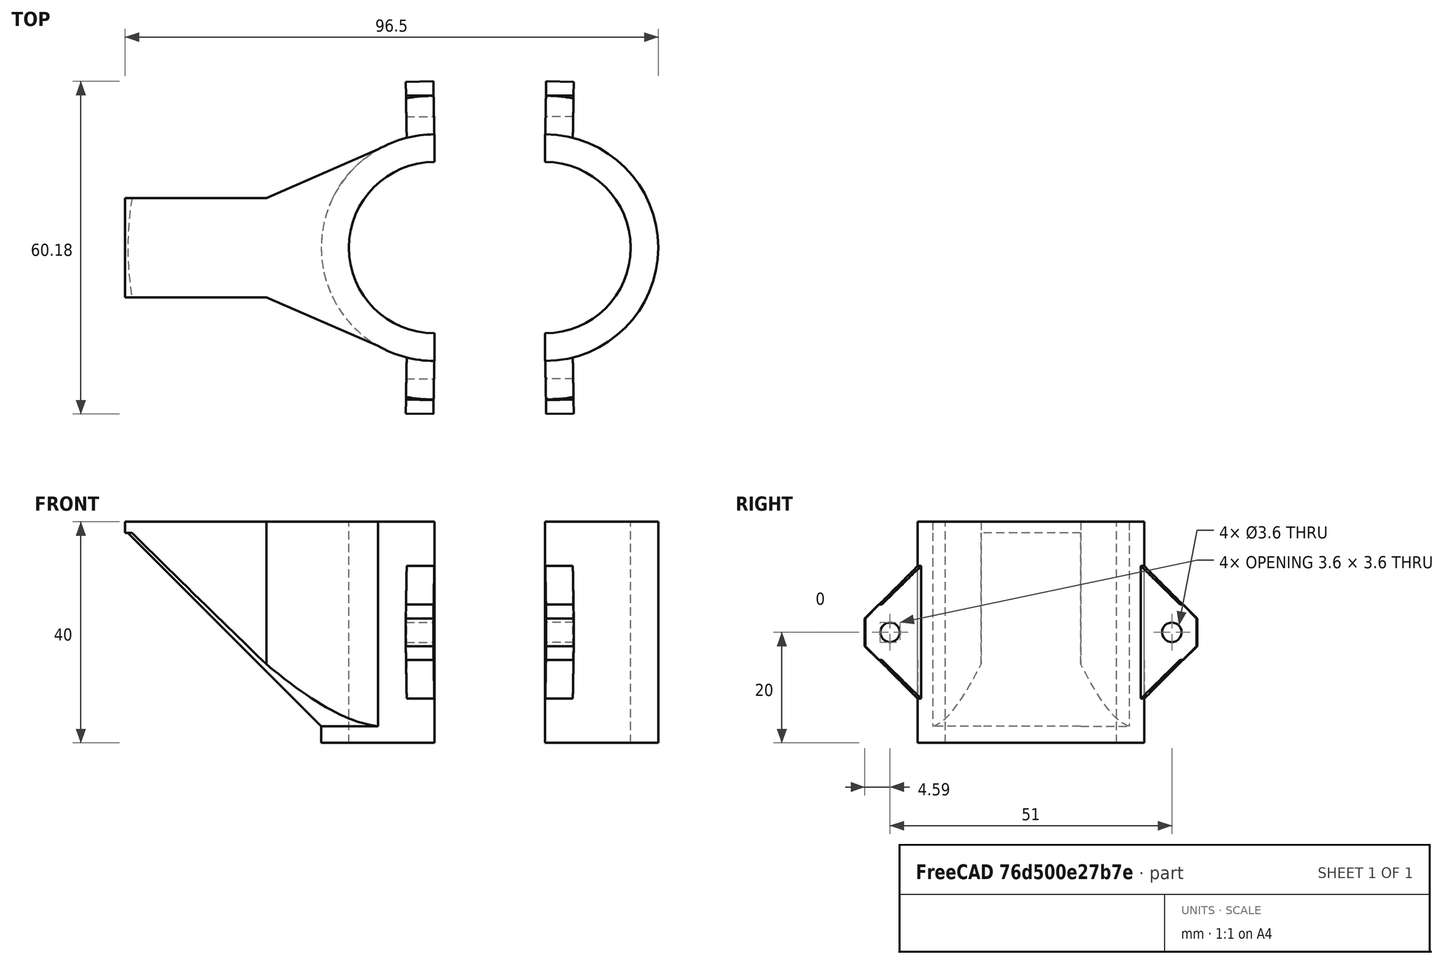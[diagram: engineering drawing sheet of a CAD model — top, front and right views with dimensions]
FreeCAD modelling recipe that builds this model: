
FCSTD DOCUMENT  (FreeCAD 0.17R13528 (Git))
Label: soporteBalda
License: All rights reserved
LicenseURL: http://en.wikipedia.org/wiki/All_rights_reserved
objects: Part::Chamfer×6, Part::Cylinder×3, Part::Cut×3, Part::Box×3, Part::MultiFuse×3, Spreadsheet::Sheet×1
note: 18 computed .brp shape members not serialized (recipe doc carries the construction recipe); baked Part::Feature solids carry a one-line shape summary decoded from their .brp

FEATURE [Spreadsheet::Sheet] Spreadsheet
  cells = A1=Leg diameter; B1(legDiameter)=31; A2=Total height; B2(height)=40
FEATURE [Part::Cylinder] Cylinder  label="Cilindro"
  Angle = 360
  AttacherType = Attacher::AttachEngine3D
  Height = 40
  Radius = 20.5
  expr: Height = Spreadsheet.height
  expr: Radius = Spreadsheet.legDiameter * 0.5 + 5
FEATURE [Part::Cylinder] Cylinder001  label="Cilindro001"
  Angle = 360
  AttacherType = Attacher::AttachEngine3D
  Height = 50
  Placement = pos=(0,0,-5) rot=(0,0,1;0rad)
  Radius = 15.5
  expr: Height = Spreadsheet.height + 10
  expr: Radius = Spreadsheet.legDiameter * 0.5
FEATURE [Part::Cut] Cut
  Base = -> Cylinder
  Tool = -> Cylinder001
FEATURE [Part::Box] Box  label="Cubo"
  AttacherType = Attacher::AttachEngine3D
  Height = 50
  Length = 61
  Placement = pos=(0,-30.5,-5) rot=(0,0,1;0rad)
  Width = 61
  expr: Height = Spreadsheet.height + 10
  expr: Length = Spreadsheet.legDiameter + 30
  expr: Placement.Base.y = -(Spreadsheet.legDiameter + 30) * 0.5
  expr: Width = Spreadsheet.legDiameter + 30
FEATURE [Part::Cut] Cut001
  Base = -> Cut
  Tool = -> Box
FEATURE [Part::Box] Box001  label="Cubo001"
  AttacherType = Attacher::AttachEngine3D
  Height = 10
  Length = 5
  Placement = pos=(-5,18,15) rot=(0,0,1;0.017453rad)
  Width = 12
  expr: Placement.Base.y = Spreadsheet.legDiameter * 0.5 + 2.5
  expr: Placement.Base.z = Spreadsheet.height * 0.5 - 5
FEATURE [Part::Cylinder] Cylinder002  label="Cilindro002"
  Angle = 360
  AttacherType = Attacher::AttachEngine3D
  Height = 10
  Placement = pos=(-7,25.5,20) rot=(0,1,0;1.5708rad)
  Radius = 1.8
  expr: Placement.Base.z = Spreadsheet.height * 0.5
  expr: Placement.Base.y = Spreadsheet.legDiameter * 0.5 + 10
FEATURE [Part::Cut] Cut002
  Base = -> Box001
  Tool = -> Cylinder002
FEATURE [Part::Chamfer] Chamfer
  Base = -> Cut002
  Edges = 2 edges r=2.5: [Edge9,Edge11]
FEATURE [Part::Chamfer] Chamfer001
  Base = -> Cut002
  Edges = 2 edges r=2.5: [Edge9,Edge11]
  Placement = pos=(0,0,40) rot=(1,0,0;3.14159rad)
  expr: Placement.Base.z = Spreadsheet.height
FEATURE [Part::MultiFuse] Fusion
  Shapes = -> [Cut001,Chamfer001,Chamfer]
FEATURE [Part::Chamfer] Chamfer002
  Base = -> Fusion
  Edges = 4 edges r=7: [Edge5,Edge7,Edge10,Edge12]
FEATURE [Part::MultiFuse] Fusion001
  Shapes = -> [Cut001,Chamfer001,Chamfer]
FEATURE [Part::Chamfer] Chamfer003  label="Bracket"
  Base = -> Fusion001
  Edges = 4 edges r=7: [Edge5,Edge7,Edge10,Edge12]
  Placement = pos=(20,0,0) rot=(0,0,1;3.14159rad)
FEATURE [Part::Box] Box002  label="Cubo002"
  AttacherType = Attacher::AttachEngine3D
  Height = 2
  Length = 38
  Placement = pos=(-18,9,38) rot=(0,0,1;3.14159rad)
  Width = 18
  expr: Length = Spreadsheet.height - 2
  expr: Placement.Base.z = Spreadsheet.height - 2
  expr: Height = 2
  expr: Placement.Base.x = -(Spreadsheet.legDiameter * 0.5 + 2.5)
FEATURE [Part::MultiFuse] Fusion002
  Shapes = -> [Chamfer002,Box002]
FEATURE [Part::Chamfer] Chamfer004
  Base = -> Fusion002
  Edges = 1 edges r=35: [Edge19]
FEATURE [Part::Chamfer] Chamfer005
  Base = -> Chamfer004
  Edges = 4 edges r=12: [Edge1,Edge2,Edge5,Edge7]
